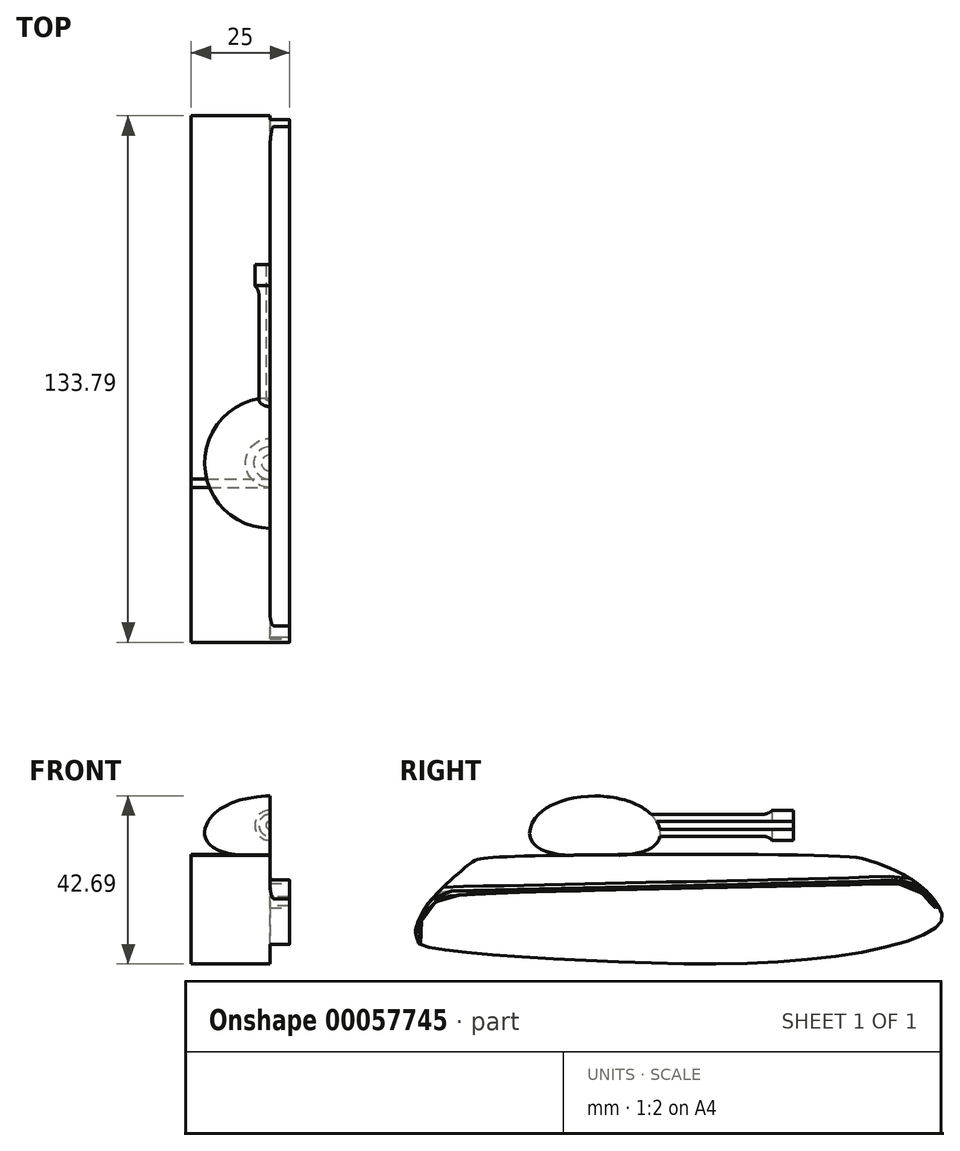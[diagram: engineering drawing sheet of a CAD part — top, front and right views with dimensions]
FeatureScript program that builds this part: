
annotation { "Feature Type Name" : "Feature", "Feature Type Description" : "" }
export const myFeature = defineFeature(function(context is Context, id is Id, definition is map)
    precondition{}
    {
        {
            var Q0;
            Q0=qCreatedBy(makeId("Right.planeOp"),FACE);
            var sketch = newSketch(context, id + "F0", { "sketchPlane" : qUnion([Q0])});
            skCircle(sketch, "E0", {"center": v(-28.96, -3.17) * mm, "radius": 5 * mm});
            skCircle(sketch, "E1", {"center": v(-2.58, -4.3) * mm, "radius": 5 * mm});
            skCircle(sketch, "E2", {"center": v(39.7, -1.22) * mm, "radius": 5 * mm});
            skCircle(sketch, "E3", {"center": v(-18.18, -4.4) * mm, "radius": 5 * mm});
            skCircle(sketch, "E4", {"center": v(-10.3, -4.22) * mm, "radius": 5 * mm});
            skCircle(sketch, "E5", {"center": v(5.45, -4.3) * mm, "radius": 5 * mm});
            skCircle(sketch, "E6", {"center": v(13.65, -4.38) * mm, "radius": 5 * mm});
            skCircle(sketch, "E7", {"center": v(21.76, -4.3) * mm, "radius": 5 * mm});
            skCircle(sketch, "E8", {"center": v(30, -3.33) * mm, "radius": 5 * mm});
            skCircle(sketch, "E9", {"center": v(-23.68, -3.72) * mm, "radius": 5 * mm});
            skFitSpline(sketch, "E10", {"points": [v(-24.17, -9.89) * mm, v(-31.03, -7.92) * mm, v(-32.53, -6.92) * mm, v(-33.27, -6.1) * mm, v(-33.97, -4.52) * mm, v(-34.12, -2.96) * mm, v(-33.94, -1.56) * mm, v(-32.9, 0.38) * mm, v(-30.87, 1.84) * mm, v(-29.21, 2.25) * mm, v(-21.63, 2.4) * mm, v(-13.26, 2.7) * mm, v(0.23, 3.13) * mm, v(12.27, 3.48) * mm, v(21.47, 3.78) * mm, v(33.09, 4.1) * mm, v(40.9, 4.3) * mm, v(43.62, 3.13) * mm, v(44.92, 1.76) * mm, v(45.6, 0.14) * mm, v(45.77, -1.5) * mm, v(45.48, -3) * mm, v(44.3, -5.04) * mm, v(42.31, -6.55) * mm, v(39.76, -7.29) * mm, v(33.79, -9.01) * mm, v(30.2, -9.88) * mm, v(27.4, -9.9) * mm, v(15.87, -9.91) * mm, v(8.9, -9.95) * mm, v(0.58, -9.94) * mm, v(-6.07, -9.92) * mm, v(-23.25, -9.9) * mm, v(-24, -9.9) * mm, v(-24.17, -9.89) * mm]});
            skFitSpline(sketch, "E11", {"points": [v(36.24, 2.39) * mm, v(-29.3, 0.64) * mm, v(-31.26, -0.5) * mm, v(-31.92, -1.76) * mm, v(-32.1, -3.51) * mm, v(-31.2, -5.66) * mm, v(-24.35, -8.14) * mm, v(-14.07, -8.25) * mm, v(26.48, -8.3) * mm, v(38.18, -5.98) * mm], "startDerivative": vector(-329.05, -3.13) * mm, "endDerivative": vector(74.4, 23.16) * mm});
            skSolve(sketch);
        }
        {
            var Q0;
            Q0=qCreatedBy(makeId("Right.planeOp"),FACE);
            var sketch = newSketch(context, id + "F1", { "sketchPlane" : qUnion([Q0])});
            skFitSpline(sketch, "E12", {"points": [v(59.07, 13.45) * mm, v(69.37, 8.54) * mm, v(75.89, 1.47) * mm, v(75.78, -2.32) * mm, v(50.58, -10.36) * mm, v(-18.72, -11.34) * mm, v(-56.13, -7.54) * mm, v(-56.76, -6.63) * mm, v(-57.35, -4.31) * mm, v(-55.94, 0) * mm, v(-53.19, 4.08) * mm, v(-43.95, 12.67) * mm, v(-37.22, 14.65) * mm, v(49.13, 14.97) * mm, v(59.07, 13.45) * mm]});
            skFitSpline(sketch, "E13", {"points": [v(-56.13, -7.54) * mm, v(-56.32, -5.68) * mm, v(-56.13, -2.34) * mm, v(-53.65, 2.1) * mm, v(-51.23, 4.01) * mm, v(-46.61, 5) * mm, v(59.02, 7.83) * mm, v(63.02, 8) * mm, v(66.47, 7.78) * mm, v(69, 6.85) * mm, v(73, 3.72) * mm, v(74.64, 1.8) * mm, v(75.47, 2.25) * mm], "startDerivative": vector(20.98, 23.71) * mm, "endDerivative": vector(29.62, 12.52) * mm});
            skFitSpline(sketch, "E14", {"points": [v(-53.19, 4.08) * mm, v(-50.43, 5.92) * mm, v(-46.7, 6.18) * mm, v(58.95, 8.66) * mm, v(62.83, 8.83) * mm, v(66.61, 8.66) * mm, v(69.35, 7.74) * mm, v(73.73, 4.64) * mm], "startDerivative": vector(59.6, 46.87) * mm, "endDerivative": vector(42, -39.14) * mm});
            skLineSegment(sketch, "E15", {"start": v(-11.78, 15.27) * mm, "end": v(-11.78, 41.69) * mm, "construction": true});
            skFitSpline(sketch, "E16", {"points": [v(-13.88, 15.24) * mm, v(-18.58, 15.2) * mm, v(-23.46, 15.92) * mm, v(-26.84, 17.61) * mm, v(-28.34, 20.22) * mm, v(-27.55, 23.67) * mm, v(-25.23, 26.3) * mm, v(-22.24, 28.12) * mm, v(-18.15, 29.48) * mm, v(-11.78, 30.27) * mm], "startDerivative": vector(-41.95, 0.4) * mm, "endDerivative": vector(39.1, 1.03) * mm});
            skLineSegment(sketch, "E17", {"start": v(-11.78, 15.27) * mm, "end": v(-11.78, 30.27) * mm});
            skLineSegment(sketch, "E18", {"start": v(-11.78, 22.77) * mm, "end": v(89.65, 22.77) * mm});
            skLineSegment(sketch, "E19", {"start": v(-11.78, 19.97) * mm, "end": v(33.22, 19.97) * mm});
            skLineSegment(sketch, "E20", {"start": v(33.22, 19.97) * mm, "end": v(33.22, 18.92) * mm});
            skLineSegment(sketch, "E21", {"start": v(33.22, 18.92) * mm, "end": v(38.63, 18.92) * mm});
            skLineSegment(sketch, "E22", {"start": v(38.63, 18.92) * mm, "end": v(38.63, 22.77) * mm});
            skLineSegment(sketch, "E23", {"start": v(-11.78, 21.77) * mm, "end": v(38.63, 21.77) * mm});
            skSolve(sketch);
        }
        {
            var Q0;
            {var subQ4=sQuery(id+"F1.wireOp",EDGE,"E17");Q0=makeQuery(id+"F1.imprint","IMPRINT",FACE,{"disambiguationData":[TD([[makeQuery(id+"F1.imprint","IMPRINT",EDGE,{"derivedFrom":subQ4}),1.0]])]});}
            var Q1;
            Q1=sQuery(id+"F1.wireOp",EDGE,"E15");
            revolve(context, id + "F2", {"entities" : qUnion([Q0]), "axis" : qUnion([Q1]), "revolveType" : RevolveType.ONE_DIRECTION, "oppositeDirection" : true, "angle" : 180 * degree});
        }
        {
            var Q0;
            {var subQ0=sQuery(id+"F1.wireOp",EDGE,"E19");Q0=makeQuery(id+"F1.imprint","IMPRINT",FACE,{"disambiguationData":[TD([[makeQuery(id+"F1.imprint","IMPRINT",EDGE,{"derivedFrom":subQ0}),1.0]])]});}
            var Q1;
            Q1=sQuery(id+"F1.wireOp",EDGE,"E18");
            revolve(context, id + "F3", {"operationType" : NewBodyOperationType.ADD, "entities" : qUnion([Q0]), "axis" : qUnion([Q1]), "revolveType" : RevolveType.ONE_DIRECTION, "angle" : 180 * degree});
        }
        {
            var Q0;
            Q0=makeQuery(id+"F3.opRevolve","SWEPT_EDGE",EDGE,{"disambiguationData":[OSD([sQuery(id+"F1.wireOp",EDGE,"E19"),sQuery(id+"F1.wireOp",EDGE,"E20")])]});
            fillet(context, id + "F4", {"entities" : qUnion([Q0]), "radius" : 3 * mm, "tangentPropagation" : true, "allowEdgeOverflow" : false});
        }
        {
            var Q0;
            {var subQ0=sQuery(id+"F1.wireOp",EDGE,"E14");Q0=makeQuery(id+"F1.imprint","IMPRINT",FACE,{"disambiguationData":[TD([[makeQuery(id+"F1.imprint","IMPRINT",EDGE,{"derivedFrom":subQ0}),1.0]])]});}
            var Q1;
            {var subQ0=sQuery(id+"F1.wireOp",EDGE,"E13");Q1=makeQuery(id+"F1.imprint","IMPRINT",FACE,{"disambiguationData":[TD([[makeQuery(id+"F1.imprint","IMPRINT",EDGE,{"derivedFrom":subQ0}),1.0]])]});}
            var Q2;
            {var subQ0=sQuery(id+"F1.wireOp",EDGE,"E13");Q2=makeQuery(id+"F1.imprint","IMPRINT",FACE,{"disambiguationData":[TD([[makeQuery(id+"F1.imprint","IMPRINT",EDGE,{"derivedFrom":subQ0}),-1.0]])]});}
            extrude(context, id + "F5", {"entities" : qUnion([Q0, Q1, Q2]), "oppositeDirection" : true, "depth" : 20 * mm});
        }
        {
            var Q0;
            {var subQ0=sQuery(id+"F1.wireOp",EDGE,"E13");Q0=makeQuery(id+"F1.imprint","IMPRINT",FACE,{"disambiguationData":[TD([[makeQuery(id+"F1.imprint","IMPRINT",EDGE,{"derivedFrom":subQ0}),1.0]])]});}
            extrude(context, id + "F6", {"entities" : qUnion([Q0]), "operationType" : NewBodyOperationType.ADD, "depth" : 5 * mm});
        }
        {
            var Q0;
            Q0=makeQuery(id+"F6.opExtrude","CAP_FACE",FACE,{"disambiguationData":[OSD([sQuery(id+"F1.wireOp",EDGE,"E12"),sQuery(id+"F1.wireOp",EDGE,"E13"),sQuery(id+"F1.wireOp",EDGE,"E14")])],"isStart":false});
            fillet(context, id + "F7", {"entities" : qUnion([Q0]), "radius" : .1 * mm, "tangentPropagation" : true, "allowEdgeOverflow" : false});
        }
        {
            var Q0;
            Q0=makeQuery(id+"F6.opExtrude","CAP_EDGE",EDGE,{"disambiguationData":[OSD([sQuery(id+"F1.wireOp",EDGE,"E14")])],"isStart":true});
            fillet(context, id + "F8", {"entities" : qUnion([Q0]), "radius" : 1 * mm, "tangentPropagation" : true, "allowEdgeOverflow" : false});
        }
    });
